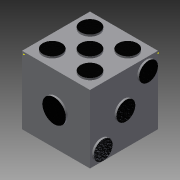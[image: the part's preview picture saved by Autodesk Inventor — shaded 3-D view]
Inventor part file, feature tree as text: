
AUTODESK INVENTOR PART (.ipt)
format: ipt  version: 2015 (Build 190159000, 159)  size: 214,528 bytes
history: native  units: in
note: dims shown in document units (in); Inventor stores cm internally (conversion verified against a paired STEP export)
features: sketch x9, extrude x7, plane x1
ambient origin geometry x8: Origin, YZ Plane, XZ Plane, XY Plane, X Axis, Y Axis, Z Axis, Center Point
bodies: Solid1 (feature_tree)
feature tree (17):
  extrude  "Extrusion1"  Depth=18.0in
  plane  "Work Plane1"
  sketch  "Sketch2"  dims[d2=18.0in d3=0.0in d4=9.0in]
  extrude  "Extrusion2"  Depth=18.0in
  sketch  "Sketch4"  dims[d21=5.0in d22=5.0in]
  extrude  "Extrusion3"  Depth=0.5in TaperAngle=0.0deg
  extrude  "Extrusion4"  Depth=5.0in
  extrude  "Extrusion5"  Depth=25.4558in
  extrude  "Extrusion6"  Depth=4.2426in
  extrude  "Extrusion7"  Depth=0.5in
  sketch  "Sketch1"  dims[d0=18.0in d1=18.0in]
  sketch  "Sketch3"  dims[d5=9.0in d6=0.5in d7=0.0in]
  sketch  "Sketch5"  dims[d23=5.0in d25=25.4558in]
  sketch  "Sketch6"  dims[d26=4.2426in d28=4.2426in]
  sketch  "Sketch7"  dims[d29=0.5in d30=0.0in d37=9.0in]
  sketch  "Sketch8"  dims[d38=4.5in]
  sketch  "Sketch9"  dims[d40=5.0in d41=5.0in d42=5.0in d43=5.0in d44=0.5in d45=0.0in d46=5.0in d47=5.0in d53=3.0in d54=3.0in d55=5.0in d56=5.0in d57=5.0in d58=5.0in d59=5.0in d60=5.0in d61=0.5in d62=0.0in d63=10.0in d64=4.0in d65=4.0in d66=4.0in d67=5.0in d68=5.0in d69=5.0in d70=5.0in d71=5.0in d72=0.5in d73=0.0in d77=25.4558in d78=5.0in d79=5.0in d80=0.5in d81=0.0in]
